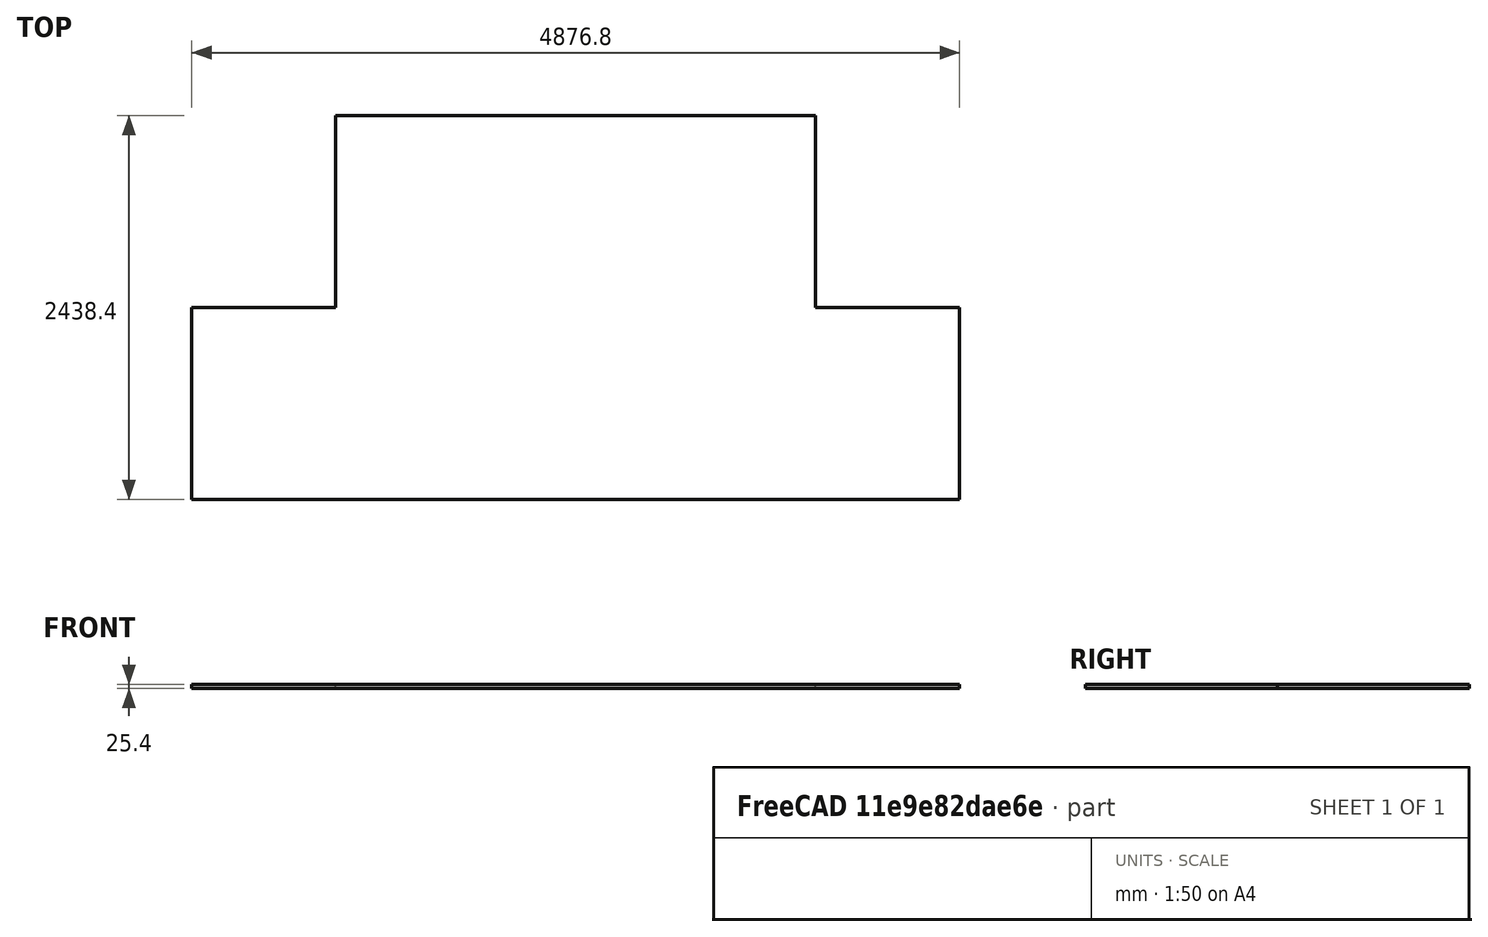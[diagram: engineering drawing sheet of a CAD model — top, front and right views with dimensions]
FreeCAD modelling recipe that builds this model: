
FCSTD DOCUMENT  (FreeCAD 0.20R29177 (Git))
Label: gazeboFootPrint
License: All rights reserved
LicenseURL: http://en.wikipedia.org/wiki/All_rights_reserved
objects: Sketcher::SketchObject×1, PartDesign::Pad×1, PartDesign::Body×1
note: 4 computed .brp shape members not serialized (recipe doc carries the construction recipe); baked Part::Feature solids carry a one-line shape summary decoded from their .brp

FEATURE [Sketcher::SketchObject] Sketch
  FullyConstrained = true
  MapMode = 5
  Support = -> [XY_Plane]
  sketch-geometry (8):
    g0: LineSegment StartX=-2438.4 StartY=-1219.2 StartZ=0 EndX=-2438.4 EndY=0 EndZ=0
    g1: LineSegment StartX=-2438.4 StartY=0 StartZ=0 EndX=-1524 EndY=0 EndZ=0
    g2: LineSegment StartX=-1524 StartY=0 StartZ=0 EndX=-1524 EndY=1219.2 EndZ=0
    g3: LineSegment StartX=-1524 StartY=1219.2 StartZ=0 EndX=1524 EndY=1219.2 EndZ=0
    g4: LineSegment StartX=1524 StartY=1219.2 StartZ=0 EndX=1524 EndY=0 EndZ=0
    g5: LineSegment StartX=1524 StartY=0 StartZ=0 EndX=2438.4 EndY=0 EndZ=0
    g6: LineSegment StartX=2438.4 StartY=0 StartZ=0 EndX=2438.4 EndY=-1219.2 EndZ=0
    g7: LineSegment StartX=2438.4 StartY=-1219.2 StartZ=0 EndX=-2438.4 EndY=-1219.2 EndZ=0
  constraints (22):
    c: Vertical(g0)
    c: Coincident(g0,g1)
    c: Horizontal(g1)
    c: Coincident(g1,g2)
    c: Vertical(g2)
    c: Coincident(g2,g3)
    c: Horizontal(g3)
    c: Coincident(g3,g4)
    c: Vertical(g4)
    c: Coincident(g4,g5)
    c: Coincident(g5,g6)
    c: Vertical(g6)
    c: Coincident(g6,g7)
    c: Coincident(g7,g0)
    c: PointOnObject(g0,g-1)
    c: DistanceX(g0,g6) = 4876.8
    c: Horizontal(g6,g0)
    c: DistanceY(g0,g0) = 1219.2
    c: DistanceY(g1,g2) = 1219.2
    c: DistanceX(g2,g3) = 3048
    c: Symmetric(g0,g5,g-1)
    c: Symmetric(g1,g4,g-1)
FEATURE [PartDesign::Pad] Pad
  Direction = (0,0,1)
  Length = 25.4
  Length2 = 9.525
  Profile = -> Sketch
  ReferenceAxis = -> Sketch [N_Axis]
  Type = 0
FEATURE [PartDesign::Body] Body
  Group = -> [Sketch,Pad]
  Origin = -> Origin
  Tip = -> Pad
